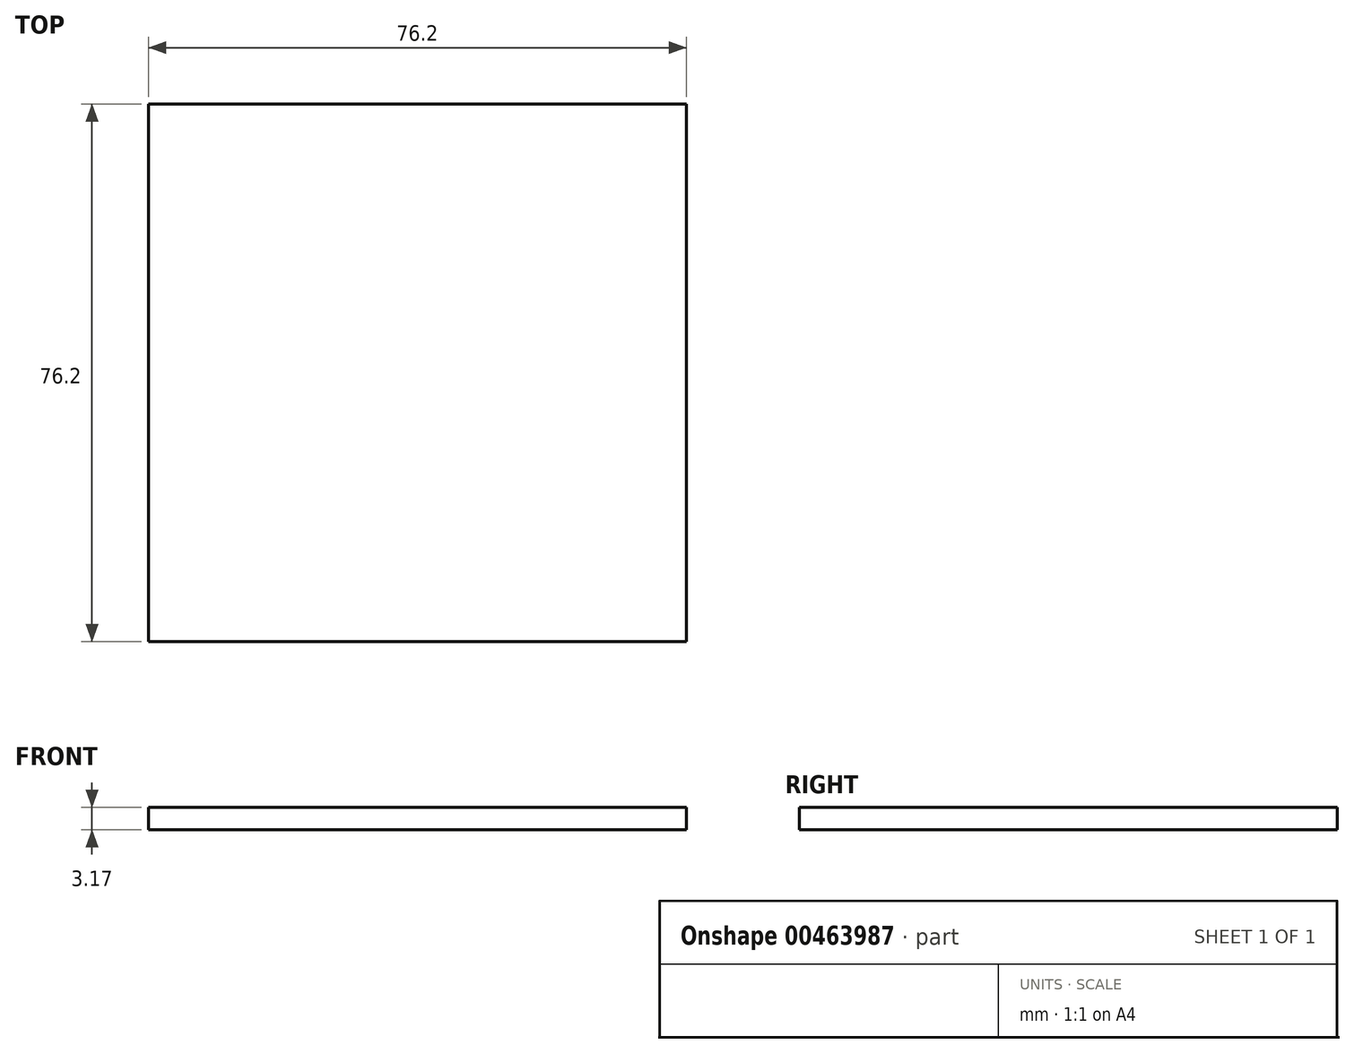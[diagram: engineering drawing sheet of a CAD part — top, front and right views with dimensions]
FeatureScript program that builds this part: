
annotation { "Feature Type Name" : "Feature", "Feature Type Description" : "" }
export const myFeature = defineFeature(function(context is Context, id is Id, definition is map)
    precondition{}
    {
        {
            var Q0;
            Q0=qCreatedBy(makeId("Top.planeOp"),FACE);
            var sketch = newSketch(context, id + "F0", { "sketchPlane" : qUnion([Q0])});
            skLineSegment(sketch, "E0.bottom", {"start": v(38.1, 38.1) * mm, "end": v(-38.1, 38.1) * mm});
            skLineSegment(sketch, "E0.top", {"start": v(38.1, -38.1) * mm, "end": v(-38.1, -38.1) * mm});
            skLineSegment(sketch, "E0.left", {"start": v(38.1, 38.1) * mm, "end": v(38.1, -38.1) * mm});
            skLineSegment(sketch, "E0.right", {"start": v(-38.1, 38.1) * mm, "end": v(-38.1, -38.1) * mm});
            skPoint(sketch, "E0.middle", {"position": v(0, 0) * mm});
            skSolve(sketch);
        }
        {
            var Q0;
            Q0 = qSketchRegion(id + "F0", true);
            extrude(context, id + "F1", {"entities" : qUnion([Q0]), "depth" : 3.17 * mm});
        }
    });
